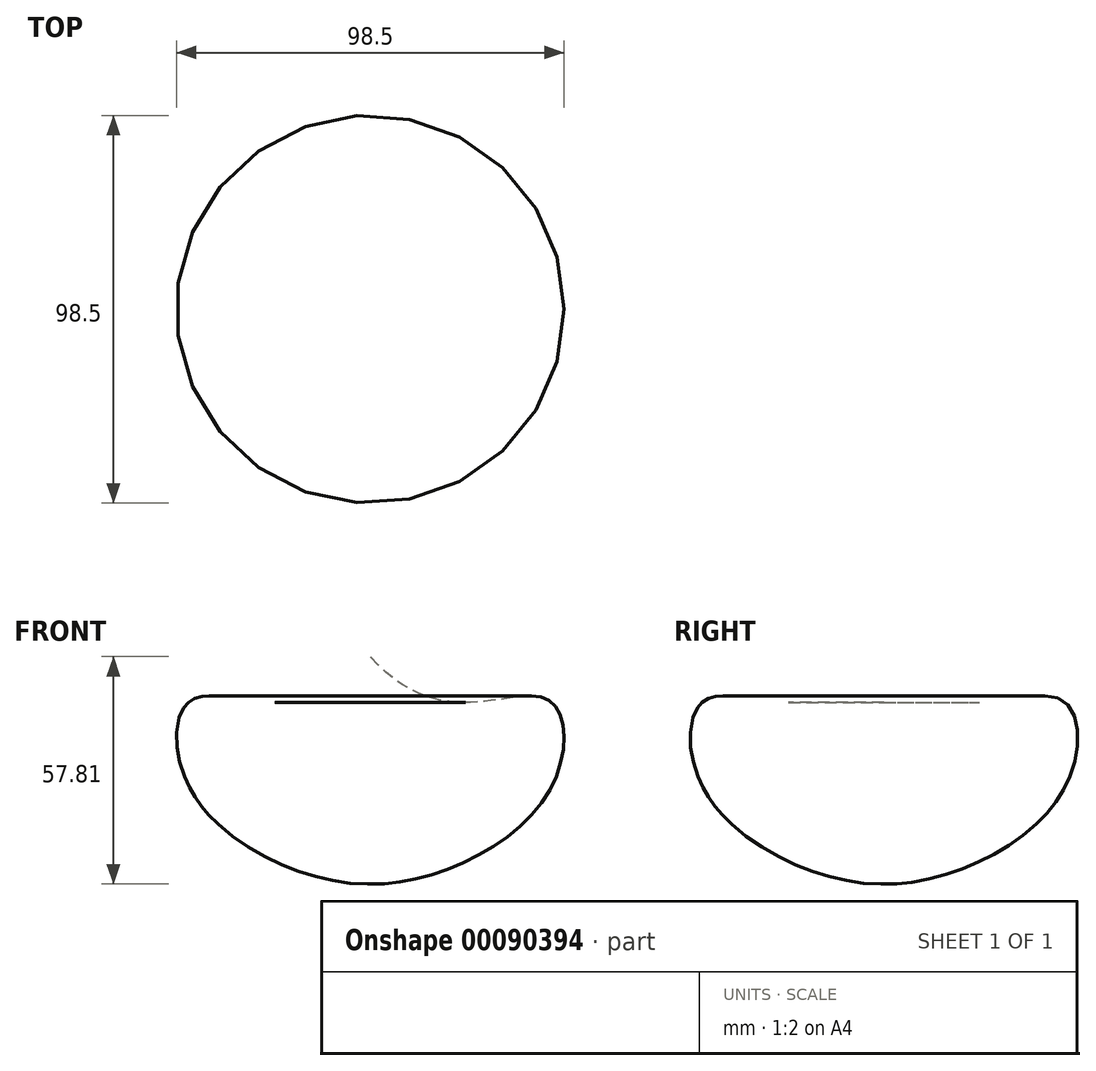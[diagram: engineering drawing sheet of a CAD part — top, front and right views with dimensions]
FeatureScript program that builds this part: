
annotation { "Feature Type Name" : "Feature", "Feature Type Description" : "" }
export const myFeature = defineFeature(function(context is Context, id is Id, definition is map)
    precondition{}
    {
        {
            var Q0;
            Q0=qCreatedBy(makeId("Front.planeOp"),FACE);
            var sketch = newSketch(context, id + "F0", { "sketchPlane" : qUnion([Q0])});
            skLineSegment(sketch, "E0.left", {"start": v(0, 0) * mm, "end": v(0, 57.8) * mm});
            skFitSpline(sketch, "E1", {"points": [v(0, 0) * mm, v(44.77, 22.48) * mm, v(44.77, 47.08) * mm, v(0, 57.8) * mm], "startDerivative": vector(118.37, -2.4) * mm, "endDerivative": vector(-149.37, 170.81) * mm});
            skSolve(sketch);
        }
        {
            var Q0;
            Q0=makeQuery(id+"F0.imprint","IMPRINT",FACE,{"disambiguationData":[TD([[makeQuery(id+"F0.imprint","IMPRINT",EDGE,{"derivedFrom":sQuery(id+"F0.wireOp",EDGE,"E0.left")}),-1.0]])]});
            var Q1;
            Q1=sQuery(id+"F0.wireOp",EDGE,"E0.left");
            revolve(context, id + "F1", {"entities" : qUnion([Q0]), "axis" : qUnion([Q1]), "revolveType" : RevolveType.FULL});
        }
    });
